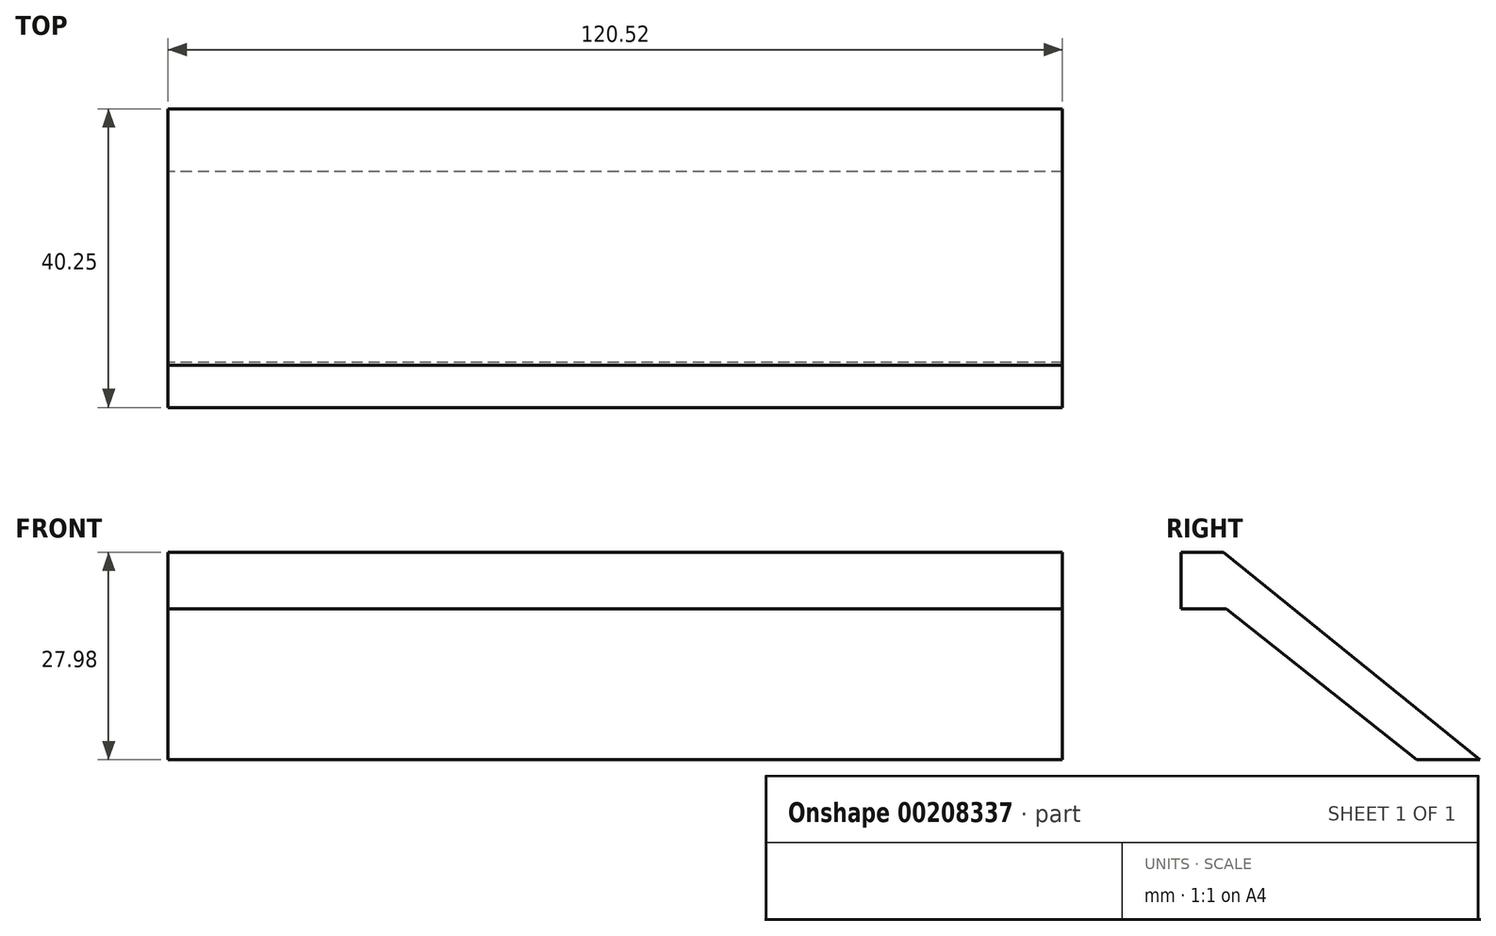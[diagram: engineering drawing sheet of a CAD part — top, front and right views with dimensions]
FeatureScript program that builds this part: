
annotation { "Feature Type Name" : "Feature", "Feature Type Description" : "" }
export const myFeature = defineFeature(function(context is Context, id is Id, definition is map)
    precondition{}
    {
        {
            var Q0;
            Q0=qCreatedBy(makeId("Right.planeOp"),FACE);
            var sketch = newSketch(context, id + "F0", { "sketchPlane" : qUnion([Q0])});
            skLineSegment(sketch, "E0", {"start": v(-45.8, 27.98) * mm, "end": v(-45.8, 20.36) * mm});
            skLineSegment(sketch, "E1", {"start": v(-45.8, 20.36) * mm, "end": v(-39.73, 20.36) * mm});
            skLineSegment(sketch, "E2", {"start": v(-39.73, 20.36) * mm, "end": v(-14.03, 0) * mm});
            skLineSegment(sketch, "E3", {"start": v(-45.8, 27.98) * mm, "end": v(-40.08, 27.98) * mm});
            skLineSegment(sketch, "E4", {"start": v(-40.08, 27.98) * mm, "end": v(-5.54, 0) * mm});
            skLineSegment(sketch, "E5", {"start": v(-5.54, 0) * mm, "end": v(-14.03, 0) * mm});
            skSolve(sketch);
        }
        {
            var Q0;
            Q0 = qSketchRegion(id + "F0", true);
            extrude(context, id + "F1", {"entities" : qUnion([Q0]), "depth" : 120.52 * mm});
        }
    });
